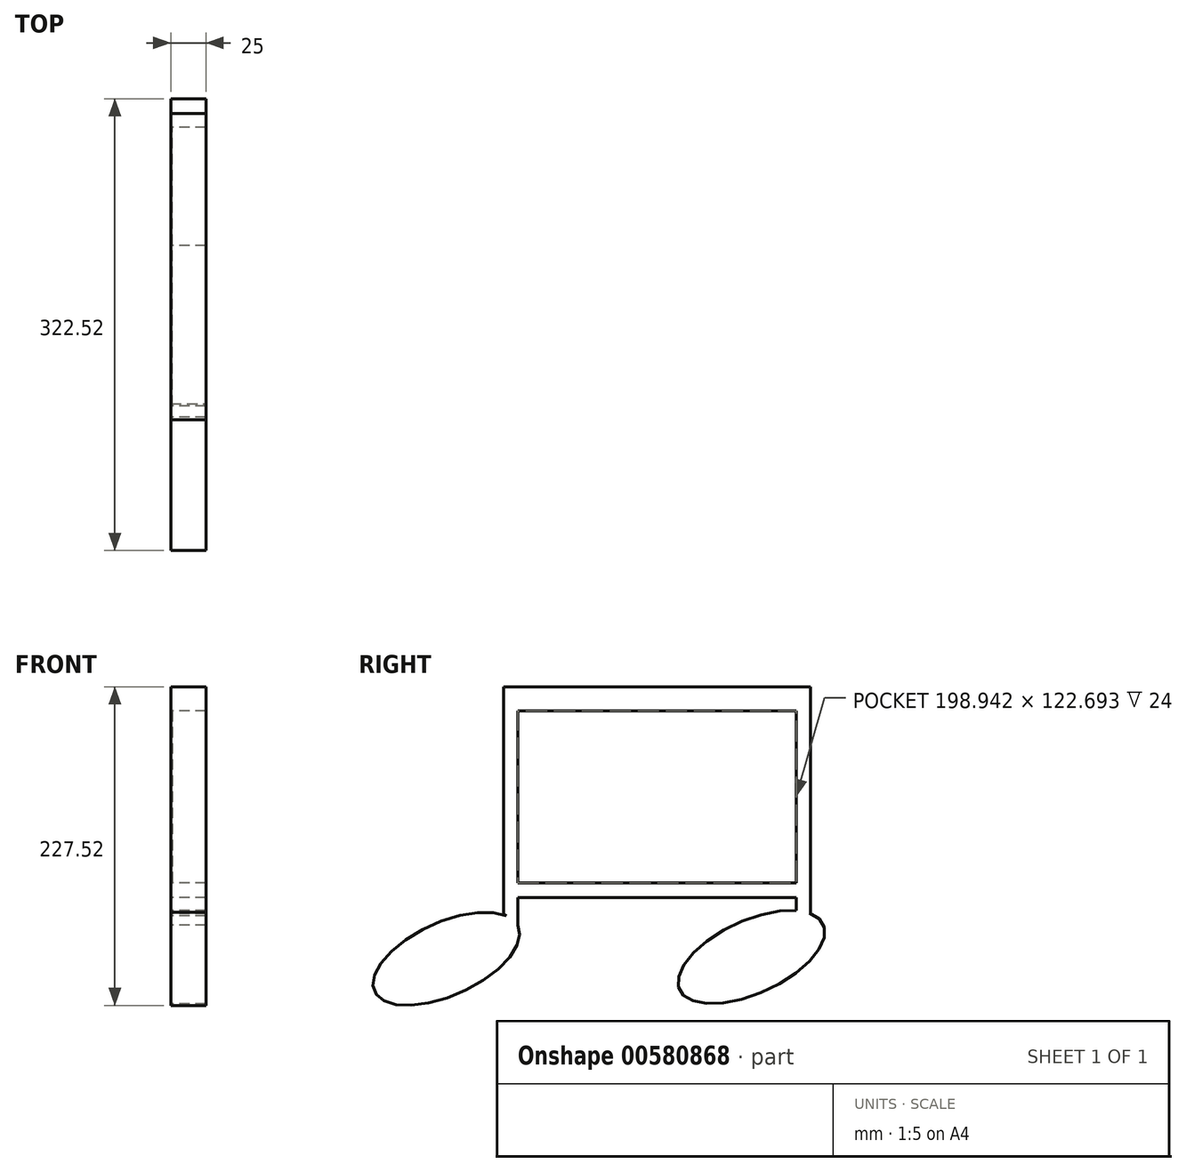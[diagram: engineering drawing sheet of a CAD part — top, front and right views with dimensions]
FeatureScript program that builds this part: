
annotation { "Feature Type Name" : "Feature", "Feature Type Description" : "" }
export const myFeature = defineFeature(function(context is Context, id is Id, definition is map)
    precondition{}
    {
        {
            var Q0;
            Q0=qCreatedBy(makeId("Right.planeOp"),FACE);
            var sketch = newSketch(context, id + "F0", { "sketchPlane" : qUnion([Q0])});
            skLineSegment(sketch, "E0", {"start": v(-34.87, 0) * mm, "end": v(-34.87, 144.6) * mm});
            skEllipse(sketch, "E1", {"center": v(-75.75, -32.42) * mm, "majorRadius": 56.3 * mm, "minorRadius": 26.15 * mm, "majorAxis": v(-0.91, -0.41)});
            skLineSegment(sketch, "E2", {"start": v(184.07, 2.26) * mm, "end": v(184.07, 144.6) * mm});
            skLineSegment(sketch, "E3", {"start": v(-34.87, 144.6) * mm, "end": v(184.07, 144.6) * mm});
            skLineSegment(sketch, "E4.bottom", {"start": v(-34.87, 161.8) * mm, "end": v(184.07, 161.8) * mm});
            skLineSegment(sketch, "E4.left", {"start": v(-34.87, 161.8) * mm, "end": v(-34.87, 144.6) * mm});
            skLineSegment(sketch, "E4.right", {"start": v(184.07, 161.8) * mm, "end": v(184.07, 144.6) * mm});
            skLineSegment(sketch, "E5.bottom", {"start": v(-34.87, 21.91) * mm, "end": v(184.07, 21.91) * mm});
            skLineSegment(sketch, "E5.top", {"start": v(-34.87, 11.15) * mm, "end": v(184.07, 11.15) * mm});
            skLineSegment(sketch, "E5.left", {"start": v(-34.87, 21.91) * mm, "end": v(-34.87, 11.15) * mm});
            skLineSegment(sketch, "E5.right", {"start": v(184.07, 21.91) * mm, "end": v(184.07, 11.15) * mm});
            skLineSegment(sketch, "E6.bottom", {"start": v(66.25, 144.6) * mm, "end": v(77.55, 144.6) * mm});
            skLineSegment(sketch, "E6.top", {"start": v(66.25, 21.91) * mm, "end": v(77.55, 21.91) * mm});
            skLineSegment(sketch, "E6.left", {"start": v(66.25, 144.6) * mm, "end": v(66.25, 21.91) * mm});
            skLineSegment(sketch, "E6.right", {"start": v(77.55, 144.6) * mm, "end": v(77.55, 21.91) * mm});
            skLineSegment(sketch, "E7.bottom", {"start": v(-34.87, 161.8) * mm, "end": v(-24.87, 161.8) * mm});
            skLineSegment(sketch, "E7.top", {"start": v(-34.87, 11.15) * mm, "end": v(-24.87, 11.15) * mm});
            skLineSegment(sketch, "E7.left", {"start": v(-34.87, 161.8) * mm, "end": v(-34.87, 11.15) * mm});
            skLineSegment(sketch, "E7.right", {"start": v(-24.87, 161.8) * mm, "end": v(-24.87, 11.15) * mm});
            skLineSegment(sketch, "E8.bottom", {"start": v(184.07, 11.15) * mm, "end": v(174.07, 11.15) * mm});
            skLineSegment(sketch, "E8.top", {"start": v(184.07, 161.8) * mm, "end": v(174.07, 161.8) * mm});
            skLineSegment(sketch, "E8.left", {"start": v(184.07, 11.15) * mm, "end": v(184.07, 161.8) * mm});
            skLineSegment(sketch, "E8.right", {"start": v(174.07, 11.15) * mm, "end": v(174.07, 161.8) * mm});
            skLineSegment(sketch, "E9", {"start": v(-24.87, 11.15) * mm, "end": v(-24.87, -8.37) * mm});
            skLineSegment(sketch, "E10", {"start": v(-24.87, -8.37) * mm, "end": v(-34.87, 0) * mm});
            skLineSegment(sketch, "E11", {"start": v(174.07, 11.15) * mm, "end": v(174.07, 5.17) * mm});
            skLineSegment(sketch, "E12", {"start": v(184.07, 2.26) * mm, "end": v(184.07, 0) * mm});
            skLineSegment(sketch, "E13", {"start": v(174.07, 5.17) * mm, "end": v(184.07, 0) * mm});
            skEllipse(sketch, "E14", {"center": v(142, -31.19) * mm, "majorRadius": 56.3 * mm, "minorRadius": 26.15 * mm, "majorAxis": v(-0.91, -0.41)});
            skLineSegment(sketch, "E15", {"start": v(174.07, 5.17) * mm, "end": v(174.07, 1.98) * mm});
            skLineSegment(sketch, "E16", {"start": v(184.07, 0) * mm, "end": v(174.07, 1.98) * mm});
            skSolve(sketch);
        }
        {
            var Q0;
            {var subQ0=sQuery(id+"F0.wireOp",EDGE,"E10");var subQ1=sQuery(id+"F0.wireOp",EDGE,"E1");var subQ3=makeQuery(id+"F0.imprint","INTERSECT",VERTEX,{"derivedFrom":[subQ1,subQ0]});Q0=qUnion([makeQuery(id+"F0.imprint","IMPRINT",FACE,{"disambiguationData":[TD([[makeQuery(id+"F0.imprint","IMPRINT",EDGE,{"disambiguationData":[TD([[subQ3,-1.0]])],"derivedFrom":subQ1}),1.0]])]}),makeQuery(id+"F0.imprint","IMPRINT",FACE,{"disambiguationData":[TD([[makeQuery(id+"F0.imprint","IMPRINT",EDGE,{"disambiguationData":[TD([[subQ3,1.0]])],"derivedFrom":subQ1}),1.0]])]})]);}
            extrude(context, id + "F1", {"entities" : qUnion([Q0]), "depth" : 25 * mm, "offsetDistance" : 25 * mm});
        }
        {
            var Q0;
            {var subQ0=sQuery(id+"F0.wireOp",EDGE,"E5.bottom");var subQ1=sQuery(id+"F0.wireOp",EDGE,"E2");var subQ2=makeQuery(id+"F0.imprint","INTERSECT",VERTEX,{"derivedFrom":[subQ1,subQ0]});var subQ7=makeQuery(id+"F0.imprint","IMPRINT",EDGE,{"disambiguationData":[TD([[subQ2,1.0]])],"derivedFrom":subQ0});var subQ8=sQuery(id+"F0.wireOp",EDGE,"E11");var subQ12=sQuery(id+"F0.wireOp",EDGE,"E4.right");var subQ13=sQuery(id+"F0.wireOp",EDGE,"E3");var subQ20=sQuery(id+"F0.wireOp",EDGE,"E6.right");var subQ21=makeQuery(id+"F0.imprint","INTERSECT",VERTEX,{"derivedFrom":[subQ13,subQ20]});var subQ29=sQuery(id+"F0.wireOp",EDGE,"E13");var subQ30=makeQuery(id+"F0.imprint","IMPRINT",EDGE,{"derivedFrom":subQ29});var subQ31=sQuery(id+"F0.wireOp",EDGE,"E0");var subQ32=makeQuery(id+"F0.imprint","INTERSECT",VERTEX,{"derivedFrom":[subQ31,subQ0]});var subQ35=makeQuery(id+"F0.imprint","IMPRINT",EDGE,{"disambiguationData":[TD([[subQ32,-1.0]])],"derivedFrom":subQ0});var subQ36=sQuery(id+"F0.wireOp",EDGE,"E9");var subQ40=makeQuery(id+"F0.imprint","INTERSECT",VERTEX,{"derivedFrom":[subQ0,subQ20]});var subQ42=sQuery(id+"F0.wireOp",EDGE,"E10");var subQ43=sQuery(id+"F0.wireOp",EDGE,"E1");var subQ45=makeQuery(id+"F0.imprint","INTERSECT",VERTEX,{"derivedFrom":[subQ43,subQ42]});var subQ46=makeQuery(id+"F0.imprint","IMPRINT",EDGE,{"disambiguationData":[TD([[subQ45,1.0]])],"derivedFrom":subQ43});var subQ48=sQuery(id+"F0.wireOp",EDGE,"E4.left");var subQ52=sQuery(id+"F0.wireOp",EDGE,"E16");var subQ54=sQuery(id+"F0.wireOp",EDGE,"E14");var subQ56=makeQuery(id+"F0.imprint","INTERSECT",VERTEX,{"derivedFrom":[subQ54,subQ52]});var subQ57=makeQuery(id+"F0.imprint","IMPRINT",EDGE,{"disambiguationData":[TD([[subQ56,-1.0]])],"derivedFrom":subQ54});Q0=qUnion([makeQuery(id+"F0.imprint","IMPRINT",FACE,{"disambiguationData":[TD([[makeQuery(id+"F0.imprint","IMPRINT",EDGE,{"derivedFrom":subQ48}),1.0]])]}),makeQuery(id+"F0.imprint","IMPRINT",FACE,{"disambiguationData":[TD([[makeQuery(id+"F0.imprint","IMPRINT",EDGE,{"disambiguationData":[TD([[subQ45,-1.0]])],"derivedFrom":subQ43}),1.0]])]}),makeQuery(id+"F0.imprint","IMPRINT",FACE,{"disambiguationData":[TD([[subQ30,-1.0]])]}),makeQuery(id+"F0.imprint","IMPRINT",FACE,{"disambiguationData":[TD([[makeQuery(id+"F0.imprint","IMPRINT",EDGE,{"disambiguationData":[TD([[subQ56,1.0]])],"derivedFrom":subQ54}),1.0]])]}),makeQuery(id+"F0.imprint","IMPRINT",FACE,{"disambiguationData":[TD([[subQ57,1.0]])]}),makeQuery(id+"F0.imprint","IMPRINT",FACE,{"disambiguationData":[TD([[makeQuery(id+"F0.imprint","IMPRINT",EDGE,{"derivedFrom":subQ36}),-1.0]])]}),makeQuery(id+"F0.imprint","IMPRINT",FACE,{"disambiguationData":[TD([[subQ35,1.0]])]}),makeQuery(id+"F0.imprint","IMPRINT",FACE,{"disambiguationData":[TD([[subQ46,1.0]])]}),makeQuery(id+"F0.imprint","IMPRINT",FACE,{"disambiguationData":[TD([[makeQuery(id+"F0.imprint","IMPRINT",EDGE,{"disambiguationData":[TD([[subQ40,-1.0]])],"derivedFrom":subQ0}),-1.0]])]}),makeQuery(id+"F0.imprint","IMPRINT",FACE,{"disambiguationData":[TD([[makeQuery(id+"F0.imprint","IMPRINT",EDGE,{"disambiguationData":[TD([[subQ32,1.0]])],"derivedFrom":subQ31}),-1.0]])]}),makeQuery(id+"F0.imprint","IMPRINT",FACE,{"disambiguationData":[TD([[makeQuery(id+"F0.imprint","IMPRINT",EDGE,{"derivedFrom":subQ8}),1.0]])]}),makeQuery(id+"F0.imprint","IMPRINT",FACE,{"disambiguationData":[TD([[makeQuery(id+"F0.imprint","IMPRINT",EDGE,{"disambiguationData":[TD([[subQ21,-1.0]])],"derivedFrom":subQ13}),1.0]])]}),makeQuery(id+"F0.imprint","IMPRINT",FACE,{"disambiguationData":[TD([[subQ7,1.0]])]}),makeQuery(id+"F0.imprint","IMPRINT",FACE,{"disambiguationData":[TD([[makeQuery(id+"F0.imprint","IMPRINT",EDGE,{"derivedFrom":subQ12}),-1.0]])]}),makeQuery(id+"F0.imprint","IMPRINT",FACE,{"disambiguationData":[TD([[makeQuery(id+"F0.imprint","IMPRINT",EDGE,{"disambiguationData":[TD([[subQ2,1.0]])],"derivedFrom":subQ1}),1.0]])]})]);}
            extrude(context, id + "F2", {"entities" : qUnion([Q0]), "operationType" : NewBodyOperationType.ADD, "depth" : 25 * mm, "offsetDistance" : 25 * mm});
        }
        {
            var Q0;
            {var subQ0=sQuery(id+"F0.wireOp",EDGE,"E1");Q0=makeQuery(id+"F2.boolean.opBoolean","MERGE",FACE,{"derivedFrom":[makeQuery(id+"F1.opExtrude","CAP_FACE",FACE,{"disambiguationData":[OSD([subQ0])],"isStart":true}),makeQuery(id+"F2.opExtrude","CAP_FACE",FACE,{"disambiguationData":[OSD([sQuery(id+"F0.wireOp",EDGE,"E0"),subQ0,sQuery(id+"F0.wireOp",EDGE,"E2"),sQuery(id+"F0.wireOp",EDGE,"E3"),sQuery(id+"F0.wireOp",EDGE,"E4.bottom"),sQuery(id+"F0.wireOp",EDGE,"E4.left"),sQuery(id+"F0.wireOp",EDGE,"E4.right"),sQuery(id+"F0.wireOp",EDGE,"E5.bottom"),sQuery(id+"F0.wireOp",EDGE,"E5.top"),sQuery(id+"F0.wireOp",EDGE,"E7.right"),sQuery(id+"F0.wireOp",EDGE,"E8.right"),sQuery(id+"F0.wireOp",EDGE,"E9"),sQuery(id+"F0.wireOp",EDGE,"E10"),sQuery(id+"F0.wireOp",EDGE,"E11"),sQuery(id+"F0.wireOp",EDGE,"E12"),sQuery(id+"F0.wireOp",EDGE,"E14"),sQuery(id+"F0.wireOp",EDGE,"E15"),sQuery(id+"F0.wireOp",EDGE,"E16")])],"isStart":true})]});}
            cPlane(context, id + "F3", {"entities" : qUnion([Q0]), "cplaneType" : CPlaneType.OFFSET, "offset" : 0 * mm, "width" : 150 * mm, "height" : 150 * mm});
        }
        {
            var Q0;
            Q0=qCreatedBy(id+"F3.planeOp",FACE);
            var sketch = newSketch(context, id + "F4", { "sketchPlane" : qUnion([Q0])});
            skLineSegment(sketch, "E17.0", {"start": v(24.87, 144.6) * mm, "end": v(-174.07, 144.6) * mm});
            skLineSegment(sketch, "E18.0", {"start": v(-174.07, 21.91) * mm, "end": v(-174.07, 144.6) * mm});
            skLineSegment(sketch, "E19.0", {"start": v(24.87, 144.6) * mm, "end": v(24.87, 21.91) * mm});
            skLineSegment(sketch, "E20.0", {"start": v(24.87, 21.91) * mm, "end": v(-174.07, 21.91) * mm});
            skSolve(sketch);
        }
        {
            var Q0;
            Q0 = qSketchRegion(id + "F4", true);
            extrude(context, id + "F5", {"entities" : qUnion([Q0]), "operationType" : NewBodyOperationType.ADD, "oppositeDirection" : true, "depth" : 1 * mm, "offsetDistance" : 25 * mm});
        }
    });
